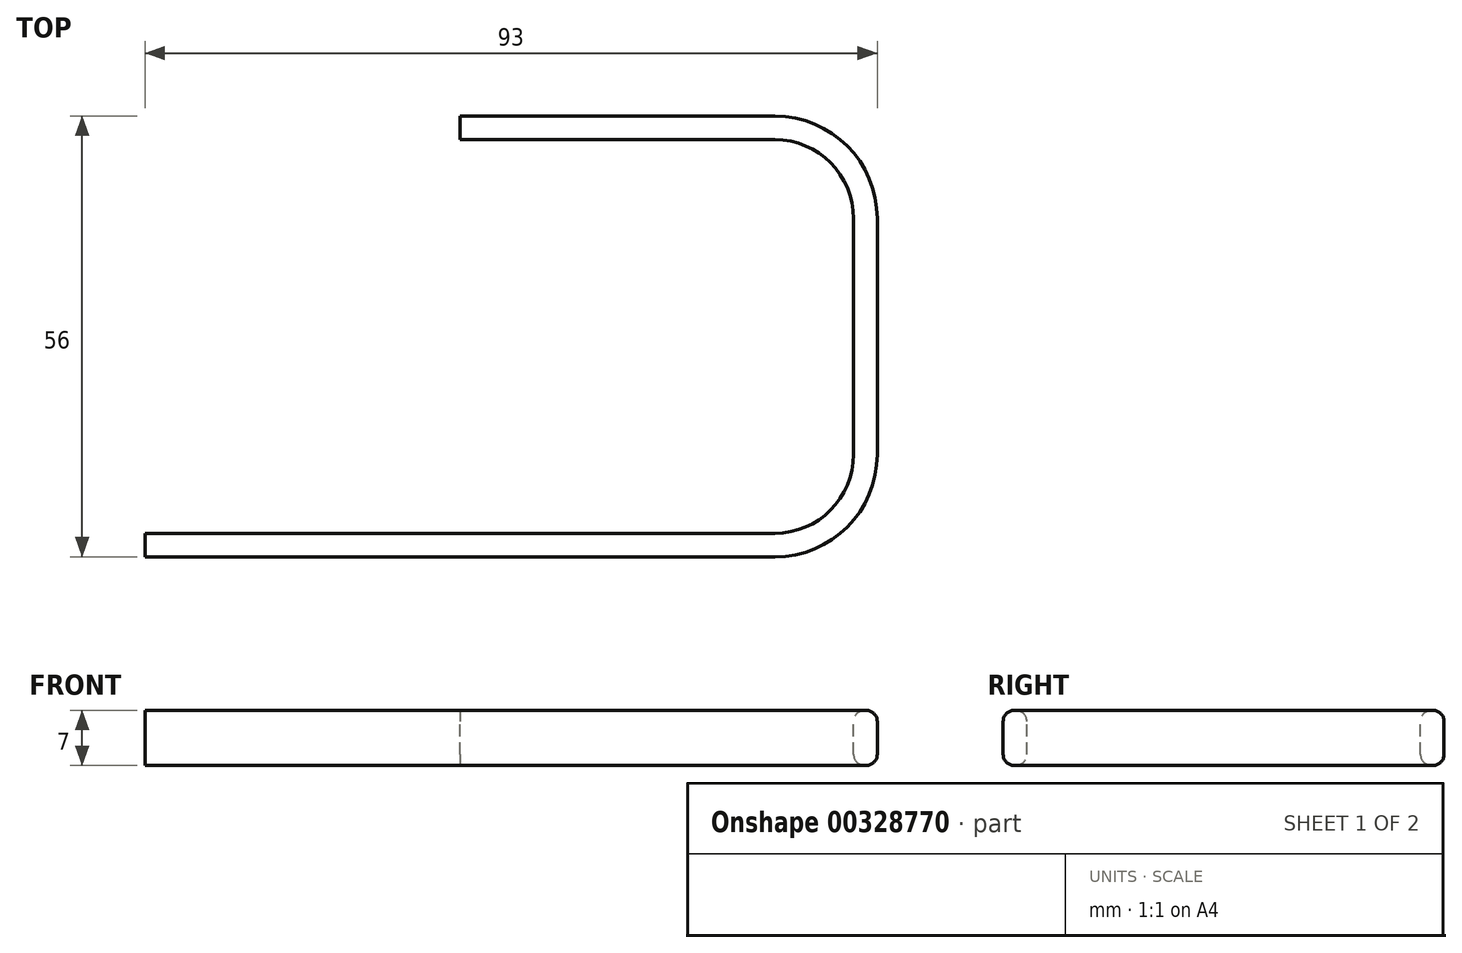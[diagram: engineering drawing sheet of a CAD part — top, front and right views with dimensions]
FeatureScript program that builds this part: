
annotation { "Feature Type Name" : "Feature", "Feature Type Description" : "" }
export const myFeature = defineFeature(function(context is Context, id is Id, definition is map)
    precondition{}
    {
        {
            var Q0;
            Q0=qCreatedBy(makeId("Right.planeOp"),FACE);
            var sketch = newSketch(context, id + "F0", { "sketchPlane" : qUnion([Q0])});
            skLineSegment(sketch, "E0.bottom", {"start": v(1.4, 0) * mm, "end": v(1.6, 0) * mm});
            skLineSegment(sketch, "E0.top", {"start": v(1.4, 7) * mm, "end": v(1.6, 7) * mm});
            skLineSegment(sketch, "E0.left", {"start": v(0, 1.4) * mm, "end": v(0, 5.6) * mm});
            skLineSegment(sketch, "E0.right", {"start": v(3, 1.4) * mm, "end": v(3, 5.6) * mm});
            skPoint(sketch, "E1.visualSharp", {"position": v(0, 7) * mm});
            skArc(sketch, "E1.filletArc", {"start": v(1.4, 7) * mm, "mid": v(0.41, 6.59) * mm, "end": v(0, 5.6) * mm});
            skPoint(sketch, "E2.visualSharp", {"position": v(3, 7) * mm});
            skArc(sketch, "E2.filletArc", {"start": v(3, 5.6) * mm, "mid": v(2.59, 6.59) * mm, "end": v(1.6, 7) * mm});
            skPoint(sketch, "E3.visualSharp", {"position": v(3, 0) * mm});
            skArc(sketch, "E3.filletArc", {"start": v(1.6, 0) * mm, "mid": v(2.59, 0.41) * mm, "end": v(3, 1.4) * mm});
            skPoint(sketch, "E4.visualSharp", {"position": v(0, 0) * mm});
            skArc(sketch, "E4.filletArc", {"start": v(0, 1.4) * mm, "mid": v(0.41, 0.41) * mm, "end": v(1.4, 0) * mm});
            skSolve(sketch);
        }
        {
            var Q0;
            Q0=qCreatedBy(makeId("Top.planeOp"),FACE);
            var sketch = newSketch(context, id + "F1", { "sketchPlane" : qUnion([Q0])});
            skLineSegment(sketch, "E5", {"start": v(0, 0) * mm, "end": v(40, 0) * mm});
            skLineSegment(sketch, "E6", {"start": v(50, -10) * mm, "end": v(50, -40) * mm});
            skLineSegment(sketch, "E7", {"start": v(40, -50) * mm, "end": v(-40, -50) * mm});
            skPoint(sketch, "E8.visualSharp", {"position": v(50, 0) * mm});
            skArc(sketch, "E8.filletArc", {"start": v(50, -10) * mm, "mid": v(47.07, -2.93) * mm, "end": v(40, 0) * mm});
            skPoint(sketch, "E9.visualSharp", {"position": v(50, -50) * mm});
            skArc(sketch, "E9.filletArc", {"start": v(40, -50) * mm, "mid": v(47.07, -47.07) * mm, "end": v(50, -40) * mm});
            skSolve(sketch);
        }
        {
            var Q0;
            Q0 = qSketchRegion(id + "F0", true);
            var Q1;
            Q1 = qConstructionFilter(qBodyType(qCreatedBy(id + "F1" ,EDGE), BodyType.WIRE), ConstructionObject.NO);
            sweep(context, id + "F2", {"profiles" : qUnion([Q0]), "path" : qUnion([Q1])});
        }
    });
